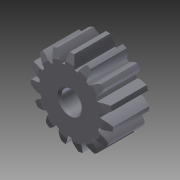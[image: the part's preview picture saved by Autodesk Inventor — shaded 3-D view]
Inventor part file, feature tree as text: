
AUTODESK INVENTOR PART (.ipt)
format: ipt  version: 2014 SP1 (Build 180222100, 222)  size: 320,512 bytes
history: native  units: mm (DEFAULTED — no unit token found)
features: other x4, plane x3, chamfer x3, sketch x3, extrude x2
ambient origin geometry x8: Origin, YZ Plane, XZ Plane, XY Plane, X Axis, Y Axis, Z Axis, Center Point
bodies: Solid1 (feature_tree)
feature tree (15):
  other  "15T Gear P60"
  extrude  "Extrusion1"  Depth=5.0mm TaperAngle=0.0deg
  plane  "Work Plane1"
  plane  "Work Plane2"
  plane  "Work Plane3"
  other  "Spur Gear"
  extrude  "Extrusion2"  Depth=76.2mm TaperAngle=0.0deg
  chamfer  "Chamfer1"  Distance=2.094395mm
  chamfer  "Chamfer2"  Distance=9.0mm
  chamfer  "Chamfer3"  [1 undecoded]
  sketch  "Sketch1"  dims[d0=10.2mm d1=5.0mm d2=0.0mm]
  sketch  "Sketch2"  dims[d3=9.0mm d4=76.2mm d5=0.0mm d6=0.0mm d7=2.094395mm]
  other  "Srf1"
  sketch  "Sketch3"  dims[d9=0.0mm d14=0.0mm d15=9.0mm d16=0.0mm d17=0.0mm d18=0.0mm d19=9.0mm d20=2.5mm d22=25.4mm d23=0.0mm d26=0.254mm d27=3.175mm d28=45.0deg d29=1.0mm d30=3.175mm d31=15.0deg d32=1.0mm d33=3.175mm d34=15.0deg]
  other  "Pitch Diameter"
note: 1 required parameter value undecoded (feature->parameter linkage not recoverable at this tier; creation-order binding heuristic only, values carry confidence <= 0.55)
